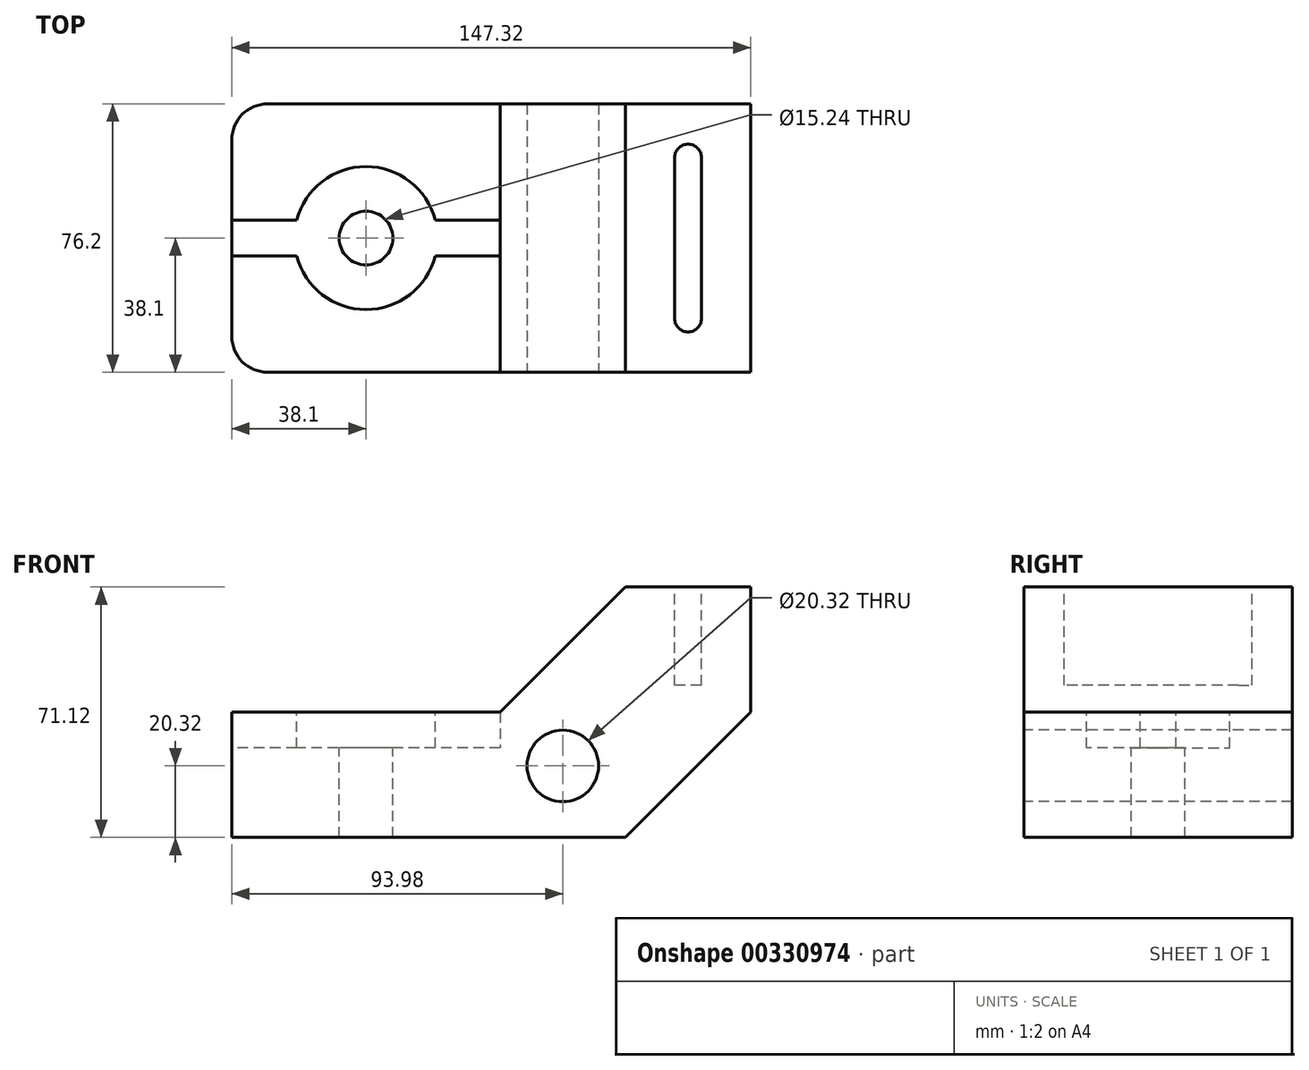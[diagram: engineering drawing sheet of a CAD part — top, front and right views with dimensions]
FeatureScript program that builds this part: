
annotation { "Feature Type Name" : "Feature", "Feature Type Description" : "" }
export const myFeature = defineFeature(function(context is Context, id is Id, definition is map)
    precondition{}
    {
        {
            var Q0;
            Q0=qCreatedBy(makeId("Front.planeOp"),FACE);
            var sketch = newSketch(context, id + "F0", { "sketchPlane" : qUnion([Q0])});
            skLineSegment(sketch, "E0", {"start": v(-55.88, 0) * mm, "end": v(55.88, 0) * mm});
            skLineSegment(sketch, "E1", {"start": v(55.88, 0) * mm, "end": v(91.44, 35.56) * mm});
            skLineSegment(sketch, "E2", {"start": v(91.44, 35.56) * mm, "end": v(91.44, 71.12) * mm});
            skLineSegment(sketch, "E3", {"start": v(91.44, 71.12) * mm, "end": v(55.88, 71.12) * mm});
            skLineSegment(sketch, "E4", {"start": v(55.88, 71.12) * mm, "end": v(20.32, 35.56) * mm});
            skLineSegment(sketch, "E5", {"start": v(20.32, 35.56) * mm, "end": v(-55.88, 35.56) * mm});
            skLineSegment(sketch, "E6", {"start": v(-55.88, 35.56) * mm, "end": v(-55.88, 0) * mm});
            skSolve(sketch);
        }
        {
            var Q0;
            Q0=makeQuery(id+"F0.imprint","IMPRINT",FACE,{"disambiguationData":[TD([[makeQuery(id+"F0.imprint","IMPRINT",EDGE,{"derivedFrom":sQuery(id+"F0.wireOp",EDGE,"E0")}),1.0]])]});
            extrude(context, id + "F1", {"entities" : qUnion([Q0]), "depth" : 76.2 * mm});
        }
        {
            var Q0;
            Q0=makeQuery(id+"F1.opExtrude","CAP_FACE",FACE,{"disambiguationData":[OSD([sQuery(id+"F0.wireOp",EDGE,"E0"),sQuery(id+"F0.wireOp",EDGE,"E1"),sQuery(id+"F0.wireOp",EDGE,"E2"),sQuery(id+"F0.wireOp",EDGE,"E3"),sQuery(id+"F0.wireOp",EDGE,"E4"),sQuery(id+"F0.wireOp",EDGE,"E5"),sQuery(id+"F0.wireOp",EDGE,"E6")])],"isStart":false});
            var sketch = newSketch(context, id + "F2", { "sketchPlane" : qUnion([Q0])});
            skCircle(sketch, "E7", {"center": v(38.1, 20.32) * mm, "radius": 10.16 * mm});
            skSolve(sketch);
        }
        {
            var Q0;
            Q0 = qSketchRegion(id + "F2", true);
            extrude(context, id + "F3", {"entities" : qUnion([Q0]), "operationType" : NewBodyOperationType.REMOVE, "endBound" : BoundingType.THROUGH_ALL, "oppositeDirection" : true, "depth" : 25.4 * mm});
        }
        {
            var Q0;
            Q0=makeQuery(id+"F1.opExtrude","SWEPT_FACE",FACE,{"disambiguationData":[OSD([sQuery(id+"F0.wireOp",EDGE,"E6")])]});
            var sketch = newSketch(context, id + "F4", { "sketchPlane" : qUnion([Q0])});
            skLineSegment(sketch, "E8.bottom", {"start": v(33.02, 35.56) * mm, "end": v(43.18, 35.56) * mm});
            skLineSegment(sketch, "E8.top", {"start": v(33.02, 25.4) * mm, "end": v(43.18, 25.4) * mm});
            skLineSegment(sketch, "E8.left", {"start": v(33.02, 35.56) * mm, "end": v(33.02, 25.4) * mm});
            skLineSegment(sketch, "E8.right", {"start": v(43.18, 35.56) * mm, "end": v(43.18, 25.4) * mm});
            skSolve(sketch);
        }
        {
            var Q0;
            Q0 = qSketchRegion(id + "F4", true);
            extrude(context, id + "F5", {"entities" : qUnion([Q0]), "operationType" : NewBodyOperationType.REMOVE, "oppositeDirection" : true, "depth" : 76.2 * mm});
        }
        {
            var Q0;
            {var subQ0=sQuery(id+"F4.wireOp",EDGE,"E8.left");var subQ3=sQuery(id+"F0.wireOp",EDGE,"E5");Q0=makeQuery(id+"F5.boolean.opBoolean","SPLIT",FACE,{"disambiguationData":[TD([makeQuery(id+"F5.opExtrude","SWEPT_FACE",FACE,{"disambiguationData":[OSD([subQ0])]})])],"derivedFrom":makeQuery(id+"F1.opExtrude","SWEPT_FACE",FACE,{"disambiguationData":[OSD([subQ3])]})});}
            var sketch = newSketch(context, id + "F6", { "sketchPlane" : qUnion([Q0])});
            skPoint(sketch, "E9", {"position": v(-17.78, -38.1) * mm});
            skPoint(sketch, "E9.positionSnap0", {"position": v(-17.78, -33.02) * mm});
            skSolve(sketch);
        }
        {
            var Q0;
            Q0=sQuery(id+"F6.wireOp",VERTEX,"E9");
            var Q1;
            Q1=makeQuery(id+"F1.opExtrude","SWEPT_BODY",BODY,{"disambiguationData":[OSD([sQuery(id+"F0.wireOp",EDGE,"E0"),sQuery(id+"F0.wireOp",EDGE,"E1"),sQuery(id+"F0.wireOp",EDGE,"E2"),sQuery(id+"F0.wireOp",EDGE,"E3"),sQuery(id+"F0.wireOp",EDGE,"E4"),sQuery(id+"F0.wireOp",EDGE,"E5"),sQuery(id+"F0.wireOp",EDGE,"E6")])]});
            hole(context, id + "F7", {"style" : HoleStyle.C_BORE, "endStyle" : HoleEndStyle.THROUGH, "holeDiameter" : 15.24 * mm, "cBoreDiameter" : 40.64 * mm, "cBoreDepth" : 0 * mm, "tappedDepth" : 12.7 * mm, "tapClearance" : 3, "locations" : qUnion([Q0]), "scope" : qUnion([Q1])});
        }
        {
            var Q0;
            Q0=makeQuery(id+"F1.opExtrude","SWEPT_FACE",FACE,{"disambiguationData":[OSD([sQuery(id+"F0.wireOp",EDGE,"E3")])]});
            var sketch = newSketch(context, id + "F8", { "sketchPlane" : qUnion([Q0])});
            skArc(sketch, "E10", {"start": v(77.47, -15.24) * mm, "mid": v(73.66, -11.43) * mm, "end": v(69.85, -15.24) * mm});
            skPoint(sketch, "E10.centerSnap0", {"position": v(73.66, 0) * mm});
            skArc(sketch, "E11", {"start": v(69.85, -60.96) * mm, "mid": v(73.66, -64.77) * mm, "end": v(77.47, -60.96) * mm});
            skLineSegment(sketch, "E12", {"start": v(69.85, -15.24) * mm, "end": v(69.85, -60.96) * mm});
            skLineSegment(sketch, "E13", {"start": v(77.47, -15.24) * mm, "end": v(77.47, -60.96) * mm});
            skSolve(sketch);
        }
        {
            var Q0;
            Q0=makeQuery(id+"F8.imprint","IMPRINT",FACE,{"disambiguationData":[TD([[makeQuery(id+"F8.imprint","IMPRINT",EDGE,{"derivedFrom":sQuery(id+"F8.wireOp",EDGE,"E10")}),1.0]])]});
            extrude(context, id + "F9", {"entities" : qUnion([Q0]), "operationType" : NewBodyOperationType.REMOVE, "oppositeDirection" : true, "depth" : 27.94 * mm});
        }
        {
            var Q0;
            Q0=makeQuery(id+"F1.opExtrude","CAP_EDGE",EDGE,{"disambiguationData":[OSD([sQuery(id+"F0.wireOp",EDGE,"E6")])],"isStart":false});
            var Q1;
            Q1=makeQuery(id+"F1.opExtrude","CAP_EDGE",EDGE,{"disambiguationData":[OSD([sQuery(id+"F0.wireOp",EDGE,"E6")])],"isStart":true});
            fillet(context, id + "F10", {"entities" : qUnion([Q0, Q1]), "radius" : 10.16 * mm, "tangentPropagation" : true, "allowEdgeOverflow" : false});
        }
    });
